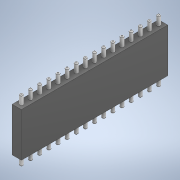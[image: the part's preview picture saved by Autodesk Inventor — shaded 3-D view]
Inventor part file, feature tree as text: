
AUTODESK INVENTOR PART (.ipt)
format: ipt  version: 2021 (Build 250183000, 183)  size: 167,936 bytes
history: native  units: in
note: dims shown in document units (in); Inventor stores cm internally (conversion verified against a paired STEP export)
features: extrude x2, sketch x2, fillet x1, pattern_linear x1, plane x1, mirror x1
ambient origin geometry x8: Origin, YZ Plane, XZ Plane, XY Plane, X Axis, Y Axis, Z Axis, Center Point
bodies: Solid1 (feature_tree)
feature tree (8):
  extrude  "Extrusion1"  Depth=0.1in
  extrude  "Extrusion2"  Depth=0.1in
  fillet  "Fillet1"  Radius=0.05in
  pattern_linear  "Rectangular Pattern1"  Spacing1=0.05in  [1 undecoded]
  plane  "Work Plane1"
  mirror  "Mirror1"
  sketch  "Sketch1"  dims[d0=1.6in d1=0.1in]
  sketch  "Sketch2"  dims[d2=0.48in d3=0.0in d4=0.0354in d5=0.05in d6=0.05in d7=0.1in d8=0.0in d9=0.01in d10=6.2992in d12=0.1in]
note: 1 required parameter value undecoded (feature->parameter linkage not recoverable at this tier; creation-order binding heuristic only, values carry confidence <= 0.55)
